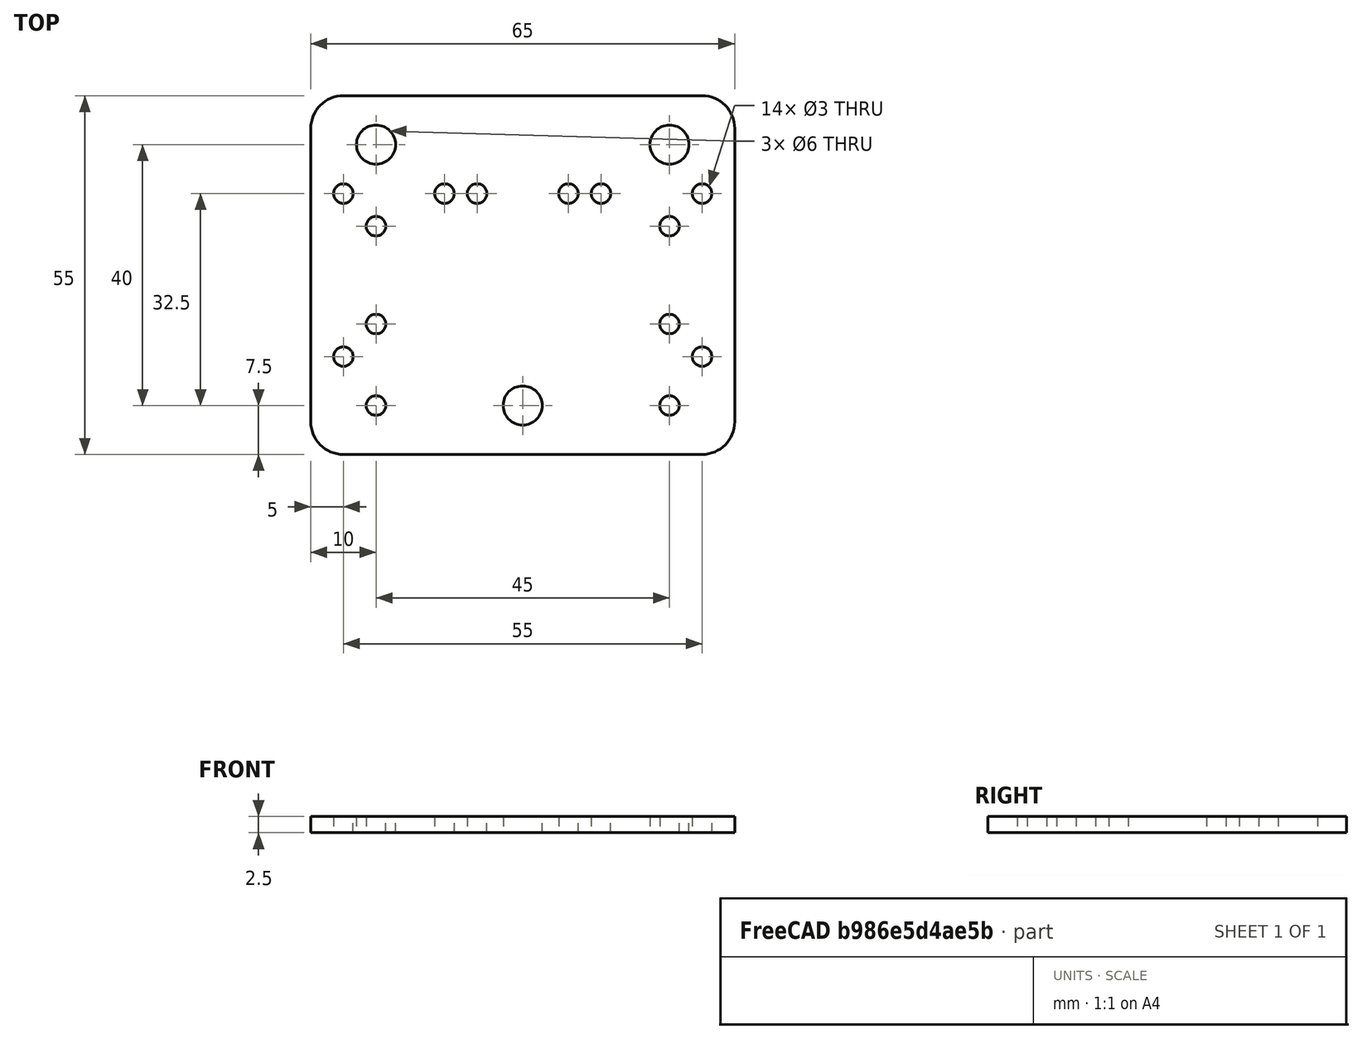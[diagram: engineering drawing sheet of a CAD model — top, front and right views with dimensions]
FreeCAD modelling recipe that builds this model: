
FCSTD DOCUMENT  (FreeCAD 0.19R24276 (Git))
Label: X_carriage
License: All rights reserved
LicenseURL: http://en.wikipedia.org/wiki/All_rights_reserved
objects: Sketcher::SketchObject×1, PartDesign::Pad×1, PartDesign::Body×1
note: 4 computed .brp shape members not serialized (recipe doc carries the construction recipe); baked Part::Feature solids carry a one-line shape summary decoded from their .brp

FEATURE [Sketcher::SketchObject] Sketch
  FullyConstrained = true
  MapMode = 5
  Support = -> [XY_Plane]
  sketch-geometry (35):
    g0: LineSegment StartX=-27.5 StartY=27.5 StartZ=0 EndX=27.5 EndY=27.5 EndZ=0
    g1: LineSegment StartX=32.5 StartY=22.5 StartZ=0 EndX=32.5 EndY=-22.5 EndZ=0
    g2: LineSegment StartX=27.5 StartY=-27.5 StartZ=0 EndX=-27.5 EndY=-27.5 EndZ=0
    g3: LineSegment StartX=-32.5 StartY=-22.5 StartZ=0 EndX=-32.5 EndY=22.5 EndZ=0
    g4: ArcOfCircle CenterX=-27.5 CenterY=22.5 CenterZ=0 NormalX=0 NormalY=0 NormalZ=1 AngleXU=0 Radius=5 StartAngle=1.5708 EndAngle=3.14159
    g5: ArcOfCircle CenterX=27.5 CenterY=22.5 CenterZ=0 NormalX=0 NormalY=0 NormalZ=1 AngleXU=0 Radius=5 StartAngle=0 EndAngle=1.5708
    g6: ArcOfCircle CenterX=27.5 CenterY=-22.5 CenterZ=0 NormalX=0 NormalY=0 NormalZ=1 AngleXU=0 Radius=5 StartAngle=4.71239 EndAngle=6.28319
    g7: ArcOfCircle CenterX=-27.5 CenterY=-22.5 CenterZ=0 NormalX=0 NormalY=0 NormalZ=1 AngleXU=0 Radius=5 StartAngle=3.14159 EndAngle=4.71239
    g8: Circle CenterX=-22.5 CenterY=20 CenterZ=0 NormalX=0 NormalY=0 NormalZ=1 AngleXU=0 Radius=3
    g9: Circle CenterX=22.5 CenterY=20 CenterZ=0 NormalX=0 NormalY=0 NormalZ=1 AngleXU=0 Radius=3
    g10: Circle CenterX=0 CenterY=-20 CenterZ=0 NormalX=0 NormalY=0 NormalZ=1 AngleXU=0 Radius=3
    g11: Circle CenterX=-12 CenterY=12.5 CenterZ=0 NormalX=0 NormalY=0 NormalZ=1 AngleXU=0 Radius=1.5
    g12: Circle CenterX=12 CenterY=12.5 CenterZ=0 NormalX=0 NormalY=0 NormalZ=1 AngleXU=0 Radius=1.5
    g13: LineSegment StartX=-32.5 StartY=12.5 StartZ=0 EndX=32.5 EndY=12.5 EndZ=0
    g14: Circle CenterX=-7 CenterY=12.5 CenterZ=0 NormalX=0 NormalY=0 NormalZ=1 AngleXU=0 Radius=1.5
    g15: Circle CenterX=7 CenterY=12.5 CenterZ=0 NormalX=0 NormalY=0 NormalZ=1 AngleXU=0 Radius=1.5
    g16: LineSegment StartX=-22.5 StartY=20 StartZ=0 EndX=22.5 EndY=20 EndZ=0
    g17: LineSegment StartX=22.5 StartY=20 StartZ=0 EndX=22.5 EndY=-20 EndZ=0
    g18: LineSegment StartX=22.5 StartY=-20 StartZ=0 EndX=-22.5 EndY=-20 EndZ=0
    g19: LineSegment StartX=-22.5 StartY=-20 StartZ=0 EndX=-22.5 EndY=20 EndZ=0
    g20: Circle CenterX=-22.5 CenterY=-20 CenterZ=0 NormalX=0 NormalY=0 NormalZ=1 AngleXU=0 Radius=1.5
    g21: Circle CenterX=22.5 CenterY=-20 CenterZ=0 NormalX=0 NormalY=0 NormalZ=1 AngleXU=0 Radius=1.5
    g22: Circle CenterX=-27.5 CenterY=12.5 CenterZ=0 NormalX=0 NormalY=0 NormalZ=1 AngleXU=0 Radius=1.5
    g23: Circle CenterX=27.5 CenterY=12.5 CenterZ=0 NormalX=0 NormalY=0 NormalZ=1 AngleXU=0 Radius=1.5
    g24: LineSegment StartX=-32.5 StartY=-12.5 StartZ=0 EndX=32.5 EndY=-12.5 EndZ=0
    g25: Circle CenterX=-27.5 CenterY=-12.5 CenterZ=0 NormalX=0 NormalY=0 NormalZ=1 AngleXU=0 Radius=1.5
    g26: Circle CenterX=27.5 CenterY=-12.5 CenterZ=0 NormalX=0 NormalY=0 NormalZ=1 AngleXU=0 Radius=1.5
    g27: Circle CenterX=-22.5 CenterY=7.5 CenterZ=0 NormalX=0 NormalY=0 NormalZ=1 AngleXU=0 Radius=1.5
    g28: Circle CenterX=-22.5 CenterY=-7.5 CenterZ=0 NormalX=0 NormalY=0 NormalZ=1 AngleXU=0 Radius=1.5
    g29: Circle CenterX=22.5 CenterY=-7.5 CenterZ=0 NormalX=0 NormalY=0 NormalZ=1 AngleXU=0 Radius=1.5
    g30: Circle CenterX=22.5 CenterY=7.5 CenterZ=0 NormalX=0 NormalY=0 NormalZ=1 AngleXU=0 Radius=1.5
    g31: LineSegment StartX=-22.5 StartY=7.5 StartZ=0 EndX=22.5 EndY=7.5 EndZ=0
    g32: LineSegment StartX=22.5 StartY=7.5 StartZ=0 EndX=22.5 EndY=-7.5 EndZ=0
    g33: LineSegment StartX=22.5 StartY=-7.5 StartZ=0 EndX=-22.5 EndY=-7.5 EndZ=0
    g34: LineSegment StartX=-22.5 StartY=-7.5 StartZ=0 EndX=-22.5 EndY=7.5 EndZ=0
  constraints (96):
    c: Horizontal(g0)
    c: Horizontal(g2)
    c: Vertical(g1)
    c: Vertical(g3)
    c: Tangent(g0,g4) = 1.5708
    c: Tangent(g3,g4) = 1.5708
    c: Tangent(g0,g5) = 1.5708
    c: Tangent(g1,g5) = 1.5708
    c: Tangent(g1,g6) = 1.5708
    c: Tangent(g2,g6) = 1.5708
    c: Tangent(g2,g7) = 1.5708
    c: Tangent(g3,g7) = 1.5708
    c: PointOnObject(g10,g-2)
    c: Symmetric(g4,g6,g-1)
    c: Equal(g7,g4)
    c: Equal(g4,g5)
    c: Equal(g5,g6)
    c: Equal(g9,g8)
    c: Equal(g8,g10)
    c: DistanceX(g3,g1) = 65
    c: Diameter(g4) = 10
    c: DistanceY(g2,g0) = 55
    c: DistanceX(g8,g9) = 45
    c: DistanceX(g8,g10) = 22.5
    c: Diameter(g8) = 6
    c: DistanceY(g-1,g8) = 20
    c: Equal(g11,g12)
    c: Diameter(g12) = 3
    c: PointOnObject(g13,g3)
    c: PointOnObject(g13,g1)
    c: Horizontal(g13)
    c: PointOnObject(g11,g13)
    c: PointOnObject(g12,g13)
    c: DistanceX(g11,g12) = 24
    c: DistanceX(g11,g-1) = 12
    c: DistanceY(g2,g13) = 40
    c: PointOnObject(g14,g13)
    c: PointOnObject(g15,g13)
    c: Equal(g15,g14)
    c: Equal(g14,g12)
    c: DistanceX(g14,g15) = 14
    c: DistanceX(g14,g-1) = 7
    c: Coincident(g16,g17)
    c: Coincident(g17,g18)
    c: Coincident(g18,g19)
    c: Coincident(g19,g16)
    c: Horizontal(g16)
    c: Horizontal(g18)
    c: Vertical(g17)
    c: Vertical(g19)
    c: Coincident(g16,g8)
    c: PointOnObject(g10,g18)
    c: Coincident(g16,g9)
    c: DistanceY(g19,g19) = 40
    c: Coincident(g20,g18)
    c: Coincident(g21,g17)
    c: Equal(g20,g21)
    c: Equal(g21,g12)
    c: PointOnObject(g22,g13)
    c: PointOnObject(g23,g13)
    c: Equal(g22,g23)
    c: Equal(g23,g12)
    c: DistanceX(g13,g22) = 5
    c: DistanceX(g23,g13) = 5
    c: PointOnObject(g24,g3)
    c: PointOnObject(g24,g1)
    c: Horizontal(g24)
    c: DistanceY(g24,g0) = 40
    c: PointOnObject(g25,g24)
    c: PointOnObject(g26,g24)
    c: Equal(g26,g25)
    c: Equal(g25,g22)
    c: DistanceX(g24,g25) = 5
    c: DistanceX(g26,g24) = 5
    c: PointOnObject(g27,g19)
    c: PointOnObject(g28,g19)
    c: PointOnObject(g29,g17)
    c: PointOnObject(g30,g17)
    c: Equal(g30,g29)
    c: Equal(g29,g28)
    c: Equal(g28,g27)
    c: Equal(g27,g11)
    c: Coincident(g31,g32)
    c: Coincident(g32,g33)
    c: Coincident(g33,g34)
    c: Coincident(g34,g31)
    c: Horizontal(g31)
    c: Horizontal(g33)
    c: Vertical(g32)
    c: Vertical(g34)
    c: Coincident(g31,g27)
    c: Coincident(g32,g29)
    c: PointOnObject(g28,g33)
    c: PointOnObject(g30,g31)
    c: DistanceY(g28,g27) = 15
    c: DistanceY(g28,g-1) = 7.5
FEATURE [PartDesign::Pad] Pad  label="HotendPlate"
  Direction = (1,1,1)
  Length = 2.5
  Length2 = 100
  Profile = -> Sketch
  Type = 0
FEATURE [PartDesign::Body] Body
  Group = -> [Sketch,Pad]
  Origin = -> Origin
  Tip = -> Pad
